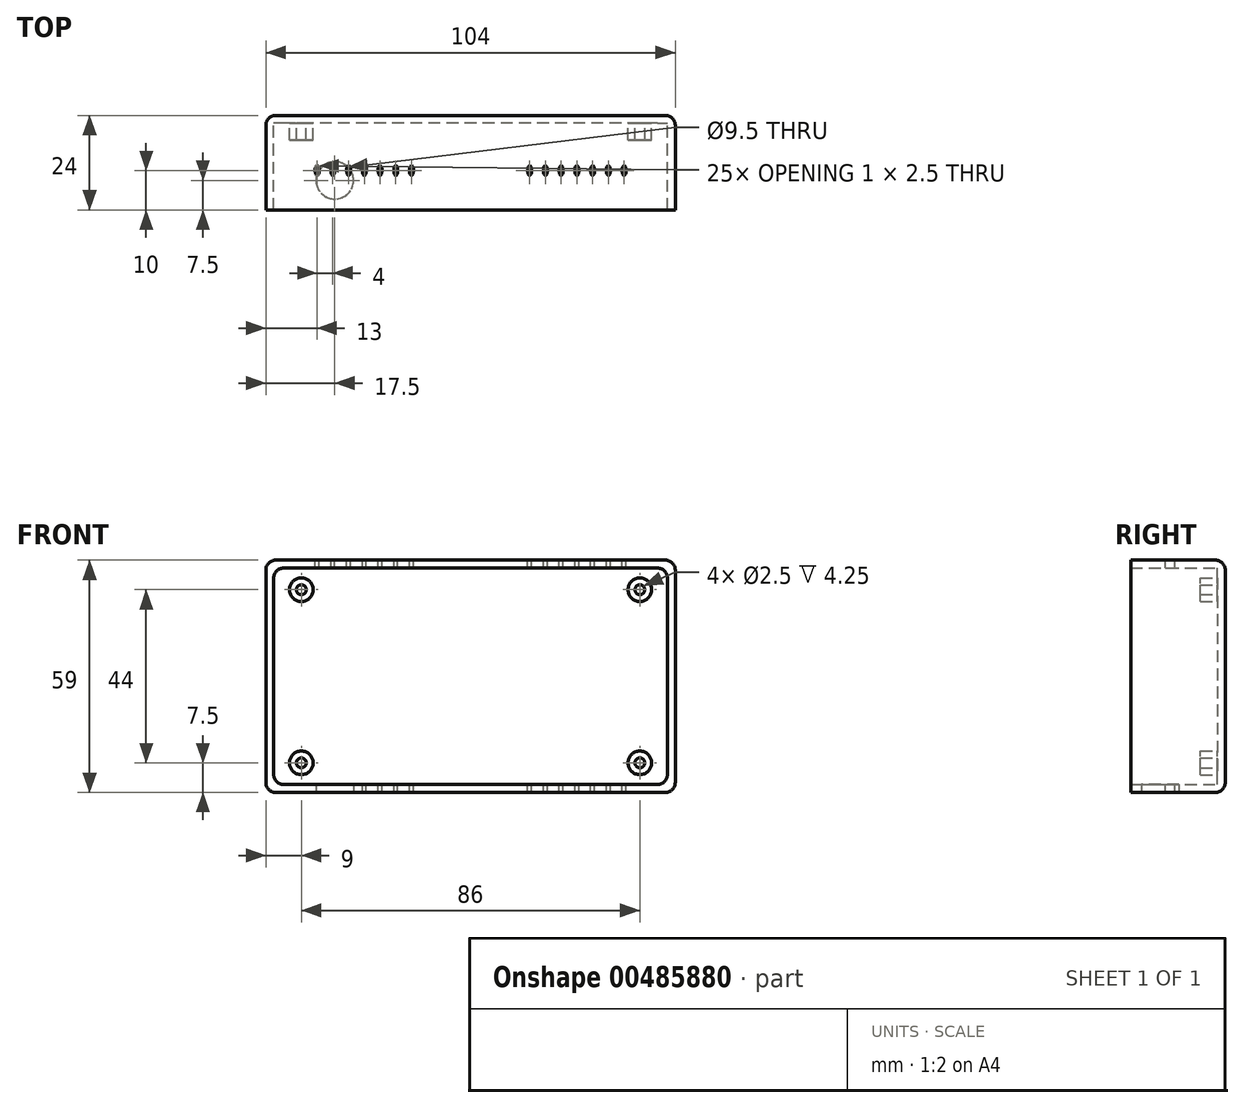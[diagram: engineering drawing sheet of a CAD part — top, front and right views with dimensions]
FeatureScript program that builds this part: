
annotation { "Feature Type Name" : "Feature", "Feature Type Description" : "" }
export const myFeature = defineFeature(function(context is Context, id is Id, definition is map)
    precondition{}
    {
        {
            var Q0;
            Q0=qCreatedBy(makeId("Front.planeOp"),FACE);
            var sketch = newSketch(context, id + "F0", { "sketchPlane" : qUnion([Q0])});
            skLineSegment(sketch, "E0.bottom", {"start": v(50, 27.5) * mm, "end": v(-50, 27.5) * mm});
            skLineSegment(sketch, "E0.top", {"start": v(50, -27.5) * mm, "end": v(-50, -27.5) * mm});
            skLineSegment(sketch, "E0.left", {"start": v(50, 27.5) * mm, "end": v(50, -27.5) * mm});
            skLineSegment(sketch, "E0.right", {"start": v(-50, 27.5) * mm, "end": v(-50, -27.5) * mm});
            skPoint(sketch, "E0.middle", {"position": v(0, 0) * mm});
            skLineSegment(sketch, "E1.bottom", {"start": v(-52, 29.5) * mm, "end": v(52, 29.5) * mm});
            skLineSegment(sketch, "E1.top", {"start": v(-52, -29.5) * mm, "end": v(52, -29.5) * mm});
            skLineSegment(sketch, "E1.left", {"start": v(-52, 29.5) * mm, "end": v(-52, -29.5) * mm});
            skLineSegment(sketch, "E1.right", {"start": v(52, 29.5) * mm, "end": v(52, -29.5) * mm});
            skSolve(sketch);
        }
        {
            var Q0;
            Q0=makeQuery(id+"F0.imprint","IMPRINT",FACE,{"disambiguationData":[TD([[makeQuery(id+"F0.imprint","IMPRINT",EDGE,{"derivedFrom":sQuery(id+"F0.wireOp",EDGE,"E0.bottom")}),1.0]])]});
            var sketch = newSketch(context, id + "F1", { "sketchPlane" : qUnion([Q0])});
            skLineSegment(sketch, "E2.bottom", {"start": v(-43, -22) * mm, "end": v(43, -22) * mm, "construction": true});
            skLineSegment(sketch, "E2.top", {"start": v(-43, 22) * mm, "end": v(43, 22) * mm, "construction": true});
            skLineSegment(sketch, "E2.left", {"start": v(-43, -22) * mm, "end": v(-43, 22) * mm, "construction": true});
            skLineSegment(sketch, "E2.right", {"start": v(43, -22) * mm, "end": v(43, 22) * mm, "construction": true});
            skPoint(sketch, "E2.middle", {"position": v(0, 0) * mm});
            skCircle(sketch, "E3", {"center": v(-43, 22) * mm, "radius": 1.25 * mm});
            skCircle(sketch, "E4", {"center": v(-43, 22) * mm, "radius": 3 * mm});
            skCircle(sketch, "E5", {"center": v(-43, -22) * mm, "radius": 1.25 * mm});
            skCircle(sketch, "E6", {"center": v(-43, -22) * mm, "radius": 3 * mm});
            skCircle(sketch, "E7", {"center": v(43, -22) * mm, "radius": 1.25 * mm});
            skCircle(sketch, "E8", {"center": v(43, -22) * mm, "radius": 3 * mm});
            skCircle(sketch, "E9", {"center": v(43, 22) * mm, "radius": 1.25 * mm});
            skCircle(sketch, "E10", {"center": v(43, 22) * mm, "radius": 3 * mm});
            skLineSegment(sketch, "E11.bottom", {"start": v(-43, -22) * mm, "end": v(-34.5, -22) * mm, "construction": true});
            skLineSegment(sketch, "E11.top", {"start": v(-43, -31.16) * mm, "end": v(-34.5, -31.16) * mm, "construction": true});
            skLineSegment(sketch, "E11.left", {"start": v(-43, -22) * mm, "end": v(-43, -31.16) * mm, "construction": true});
            skLineSegment(sketch, "E11.right", {"start": v(-34.5, -22) * mm, "end": v(-34.5, -31.16) * mm, "construction": true});
            skSolve(sketch);
        }
        {
            var Q0;
            Q0=makeQuery(id+"F0.imprint","IMPRINT",FACE,{"disambiguationData":[TD([[makeQuery(id+"F0.imprint","IMPRINT",EDGE,{"derivedFrom":sQuery(id+"F0.wireOp",EDGE,"E0.bottom")}),-1.0]])]});
            extrude(context, id + "F2", {"entities" : qUnion([Q0]), "depth" : 24 * mm, "offsetDistance" : 25 * mm});
        }
        {
            var Q0;
            Q0=makeQuery(id+"F0.imprint","IMPRINT",FACE,{"disambiguationData":[TD([[makeQuery(id+"F0.imprint","IMPRINT",EDGE,{"derivedFrom":sQuery(id+"F0.wireOp",EDGE,"E0.bottom")}),1.0]])]});
            var Q1;
            Q1=makeQuery(id+"F1.imprint","IMPRINT",FACE,{"disambiguationData":[TD([[makeQuery(id+"F1.imprint","IMPRINT",EDGE,{"derivedFrom":sQuery(id+"F1.wireOp",EDGE,"E9")}),-1.0]])]});
            var Q2;
            Q2=makeQuery(id+"F1.imprint","IMPRINT",FACE,{"disambiguationData":[TD([[makeQuery(id+"F1.imprint","IMPRINT",EDGE,{"derivedFrom":sQuery(id+"F1.wireOp",EDGE,"E4")}),-1.0]])]});
            extrude(context, id + "F3", {"entities" : qUnion([Q0, Q1, Q2]), "operationType" : NewBodyOperationType.ADD, "depth" : 2 * mm, "offsetDistance" : 25 * mm});
        }
        {
            var Q0;
            Q0=makeQuery(id+"F2.opExtrude","CAP_EDGE",EDGE,{"disambiguationData":[OSD([sQuery(id+"F0.wireOp",EDGE,"E1.top")])],"isStart":true});
            var Q1;
            Q1=makeQuery(id+"F2.opExtrude","CAP_EDGE",EDGE,{"disambiguationData":[OSD([sQuery(id+"F0.wireOp",EDGE,"E1.bottom")])],"isStart":true});
            var Q2;
            Q2=makeQuery(id+"F2.opExtrude","CAP_EDGE",EDGE,{"disambiguationData":[OSD([sQuery(id+"F0.wireOp",EDGE,"E1.left")])],"isStart":true});
            var Q3;
            Q3=makeQuery(id+"F2.opExtrude","CAP_EDGE",EDGE,{"disambiguationData":[OSD([sQuery(id+"F0.wireOp",EDGE,"E1.right")])],"isStart":true});
            fillet(context, id + "F4", {"entities" : qUnion([Q0, Q1, Q2, Q3]), "radius" : 2.5 * mm, "tangentPropagation" : true, "allowEdgeOverflow" : false});
        }
        {
            var Q0;
            Q0=makeQuery(id+"F2.opExtrude","SWEPT_EDGE",EDGE,{"disambiguationData":[OSD([sQuery(id+"F0.wireOp",EDGE,"E1.bottom"),sQuery(id+"F0.wireOp",EDGE,"E1.left")])]});
            var Q1;
            Q1=makeQuery(id+"F2.opExtrude","SWEPT_EDGE",EDGE,{"disambiguationData":[OSD([sQuery(id+"F0.wireOp",EDGE,"E1.bottom"),sQuery(id+"F0.wireOp",EDGE,"E1.right")])]});
            var Q2;
            Q2=makeQuery(id+"F2.opExtrude","SWEPT_EDGE",EDGE,{"disambiguationData":[OSD([sQuery(id+"F0.wireOp",EDGE,"E1.top"),sQuery(id+"F0.wireOp",EDGE,"E1.right")])]});
            var Q3;
            Q3=makeQuery(id+"F2.opExtrude","SWEPT_EDGE",EDGE,{"disambiguationData":[OSD([sQuery(id+"F0.wireOp",EDGE,"E1.top"),sQuery(id+"F0.wireOp",EDGE,"E1.left")])]});
            fillet(context, id + "F5", {"entities" : qUnion([Q0, Q1, Q2, Q3]), "radius" : 2.5 * mm, "tangentPropagation" : true, "allowEdgeOverflow" : false});
        }
        {
            var Q0;
            Q0=makeQuery(id+"F2.opExtrude","SWEPT_EDGE",EDGE,{"disambiguationData":[OSD([sQuery(id+"F0.wireOp",EDGE,"E0.top"),sQuery(id+"F0.wireOp",EDGE,"E0.right")])]});
            var Q1;
            Q1=makeQuery(id+"F2.opExtrude","SWEPT_EDGE",EDGE,{"disambiguationData":[OSD([sQuery(id+"F0.wireOp",EDGE,"E0.bottom"),sQuery(id+"F0.wireOp",EDGE,"E0.right")])]});
            var Q2;
            Q2=makeQuery(id+"F2.opExtrude","SWEPT_EDGE",EDGE,{"disambiguationData":[OSD([sQuery(id+"F0.wireOp",EDGE,"E0.bottom"),sQuery(id+"F0.wireOp",EDGE,"E0.left")])]});
            var Q3;
            Q3=makeQuery(id+"F2.opExtrude","SWEPT_EDGE",EDGE,{"disambiguationData":[OSD([sQuery(id+"F0.wireOp",EDGE,"E0.top"),sQuery(id+"F0.wireOp",EDGE,"E0.left")])]});
            fillet(context, id + "F6", {"entities" : qUnion([Q0, Q1, Q2, Q3]), "radius" : 2.5 * mm, "tangentPropagation" : true, "allowEdgeOverflow" : false});
        }
        {
            var Q0;
            Q0=qSketchRegion(id+"F1",true);
            extrude(context, id + "F7", {"entities" : qUnion([Q0]), "operationType" : NewBodyOperationType.ADD, "depth" : 6.25 * mm});
        }
        {
            var Q0;
            Q0=makeQuery(id+"F2.opExtrude","SWEPT_FACE",FACE,{"disambiguationData":[OSD([sQuery(id+"F0.wireOp",EDGE,"E1.bottom")])]});
            var sketch = newSketch(context, id + "F8", { "sketchPlane" : qUnion([Q0])});
            skLineSegment(sketch, "E12", {"start": v(0, 0) * mm, "end": v(0, -12) * mm});
            skEllipse(sketch, "E13", {"center": v(-39, -14) * mm, "majorRadius": 0.5 * mm, "minorRadius": 1.25 * mm, "majorAxis": v(-1, 0)});
            skEllipse(sketch, "E14", {"center": v(39, -14) * mm, "majorRadius": 0.5 * mm, "minorRadius": 1.25 * mm, "majorAxis": v(-1, 0)});
            skEllipse(sketch, "E15", {"center": v(-35, -14) * mm, "majorRadius": 0.5 * mm, "minorRadius": 1.25 * mm, "majorAxis": v(-1, 0)});
            skEllipse(sketch, "E16", {"center": v(-31, -14) * mm, "majorRadius": 0.5 * mm, "minorRadius": 1.25 * mm, "majorAxis": v(-1, 0)});
            skEllipse(sketch, "E17", {"center": v(27, -14) * mm, "majorRadius": 0.5 * mm, "minorRadius": 1.25 * mm, "majorAxis": v(-1, 0)});
            skEllipse(sketch, "E18", {"center": v(23, -14) * mm, "majorRadius": 0.5 * mm, "minorRadius": 1.25 * mm, "majorAxis": v(-1, 0)});
            skEllipse(sketch, "E19", {"center": v(19, -14) * mm, "majorRadius": 0.5 * mm, "minorRadius": 1.25 * mm, "majorAxis": v(-1, 0)});
            skEllipse(sketch, "E20", {"center": v(15, -14) * mm, "majorRadius": 0.5 * mm, "minorRadius": 1.25 * mm, "majorAxis": v(-1, 0)});
            skEllipse(sketch, "E21", {"center": v(-27, -14) * mm, "majorRadius": 0.5 * mm, "minorRadius": 1.25 * mm, "majorAxis": v(-1, 0)});
            skEllipse(sketch, "E22", {"center": v(-19, -14) * mm, "majorRadius": 0.5 * mm, "minorRadius": 1.25 * mm, "majorAxis": v(-1, 0)});
            skEllipse(sketch, "E23", {"center": v(-15, -14) * mm, "majorRadius": 0.5 * mm, "minorRadius": 1.25 * mm, "majorAxis": v(-1, 0)});
            skEllipse(sketch, "E24", {"center": v(31, -14) * mm, "majorRadius": 0.5 * mm, "minorRadius": 1.25 * mm, "majorAxis": v(-1, 0)});
            skEllipse(sketch, "E25", {"center": v(35, -14) * mm, "majorRadius": 0.5 * mm, "minorRadius": 1.25 * mm, "majorAxis": v(-1, 0)});
            skEllipse(sketch, "E26", {"center": v(-23, -14) * mm, "majorRadius": 0.5 * mm, "minorRadius": 1.25 * mm, "majorAxis": v(-1, 0)});
            skSolve(sketch);
        }
        {
            var Q0;
            Q0=makeQuery(id+"F8.imprint","IMPRINT",FACE,{"disambiguationData":[TD([[makeQuery(id+"F8.imprint","IMPRINT",EDGE,{"derivedFrom":sQuery(id+"F8.wireOp",EDGE,"E20")}),1.0]])]});
            var Q1;
            Q1=makeQuery(id+"F8.imprint","IMPRINT",FACE,{"disambiguationData":[TD([[makeQuery(id+"F8.imprint","IMPRINT",EDGE,{"derivedFrom":sQuery(id+"F8.wireOp",EDGE,"E19")}),1.0]])]});
            var Q2;
            Q2=makeQuery(id+"F8.imprint","IMPRINT",FACE,{"disambiguationData":[TD([[makeQuery(id+"F8.imprint","IMPRINT",EDGE,{"derivedFrom":sQuery(id+"F8.wireOp",EDGE,"E18")}),1.0]])]});
            var Q3;
            Q3=makeQuery(id+"F8.imprint","IMPRINT",FACE,{"disambiguationData":[TD([[makeQuery(id+"F8.imprint","IMPRINT",EDGE,{"derivedFrom":sQuery(id+"F8.wireOp",EDGE,"E17")}),1.0]])]});
            var Q4;
            Q4=makeQuery(id+"F8.imprint","IMPRINT",FACE,{"disambiguationData":[TD([[makeQuery(id+"F8.imprint","IMPRINT",EDGE,{"derivedFrom":sQuery(id+"F8.wireOp",EDGE,"E24")}),1.0]])]});
            var Q5;
            Q5=makeQuery(id+"F8.imprint","IMPRINT",FACE,{"disambiguationData":[TD([[makeQuery(id+"F8.imprint","IMPRINT",EDGE,{"derivedFrom":sQuery(id+"F8.wireOp",EDGE,"E25")}),1.0]])]});
            var Q6;
            Q6=makeQuery(id+"F8.imprint","IMPRINT",FACE,{"disambiguationData":[TD([[makeQuery(id+"F8.imprint","IMPRINT",EDGE,{"derivedFrom":sQuery(id+"F8.wireOp",EDGE,"E14")}),1.0]])]});
            var Q7;
            Q7=makeQuery(id+"F8.imprint","IMPRINT",FACE,{"disambiguationData":[TD([[makeQuery(id+"F8.imprint","IMPRINT",EDGE,{"derivedFrom":sQuery(id+"F8.wireOp",EDGE,"E23")}),1.0]])]});
            var Q8;
            Q8=makeQuery(id+"F8.imprint","IMPRINT",FACE,{"disambiguationData":[TD([[makeQuery(id+"F8.imprint","IMPRINT",EDGE,{"derivedFrom":sQuery(id+"F8.wireOp",EDGE,"E22")}),1.0]])]});
            var Q9;
            Q9=makeQuery(id+"F8.imprint","IMPRINT",FACE,{"disambiguationData":[TD([[makeQuery(id+"F8.imprint","IMPRINT",EDGE,{"derivedFrom":sQuery(id+"F8.wireOp",EDGE,"E26")}),1.0]])]});
            var Q10;
            Q10=makeQuery(id+"F8.imprint","IMPRINT",FACE,{"disambiguationData":[TD([[makeQuery(id+"F8.imprint","IMPRINT",EDGE,{"derivedFrom":sQuery(id+"F8.wireOp",EDGE,"E21")}),1.0]])]});
            var Q11;
            Q11=sQuery(id+"F8.wireOp",EDGE,"E20");
            extrude(context, id + "F9", {"entities" : qUnion([Q0, Q1, Q2, Q3, Q4, Q5, Q6, Q7, Q8, Q9, Q10]), "operationType" : NewBodyOperationType.REMOVE, "surfaceEntities" : qUnion([Q11]), "endBound" : BoundingType.THROUGH_ALL, "oppositeDirection" : true, "depth" : 25 * mm});
        }
        {
            var Q0;
            Q0=makeQuery(id+"F2.opExtrude","SWEPT_FACE",FACE,{"disambiguationData":[OSD([sQuery(id+"F0.wireOp",EDGE,"E1.top")])]});
            var sketch = newSketch(context, id + "F10", { "sketchPlane" : qUnion([Q0])});
            skLineSegment(sketch, "E27", {"start": v(-34.5, 0) * mm, "end": v(-34.5, 16.5) * mm, "construction": true});
            skCircle(sketch, "E28", {"center": v(-34.5, 16.5) * mm, "radius": 4.75 * mm});
            skSolve(sketch);
        }
        {
            var Q0;
            Q0=makeQuery(id+"F8.imprint","IMPRINT",FACE,{"disambiguationData":[TD([[makeQuery(id+"F8.imprint","IMPRINT",EDGE,{"derivedFrom":sQuery(id+"F8.wireOp",EDGE,"E16")}),1.0]])]});
            var Q1;
            Q1=makeQuery(id+"F8.imprint","IMPRINT",FACE,{"disambiguationData":[TD([[makeQuery(id+"F8.imprint","IMPRINT",EDGE,{"derivedFrom":sQuery(id+"F8.wireOp",EDGE,"E15")}),1.0]])]});
            var Q2;
            Q2=makeQuery(id+"F8.imprint","IMPRINT",FACE,{"disambiguationData":[TD([[makeQuery(id+"F8.imprint","IMPRINT",EDGE,{"derivedFrom":sQuery(id+"F8.wireOp",EDGE,"E13")}),1.0]])]});
            extrude(context, id + "F11", {"entities" : qUnion([Q0, Q1, Q2]), "operationType" : NewBodyOperationType.REMOVE, "oppositeDirection" : true, "depth" : 25 * mm, "hasSecondDirection" : true, "secondDirectionOppositeDirection" : false, "secondDirectionDepth" : 10 * mm});
        }
        {
            var Q0;
            Q0=makeQuery(id+"F10.imprint","IMPRINT",FACE,{"disambiguationData":[TD([[makeQuery(id+"F10.imprint","IMPRINT",EDGE,{"derivedFrom":sQuery(id+"F10.wireOp",EDGE,"E28")}),1.0]])]});
            extrude(context, id + "F12", {"entities" : qUnion([Q0]), "operationType" : NewBodyOperationType.REMOVE, "oppositeDirection" : true, "depth" : 10 * mm});
        }
    });
